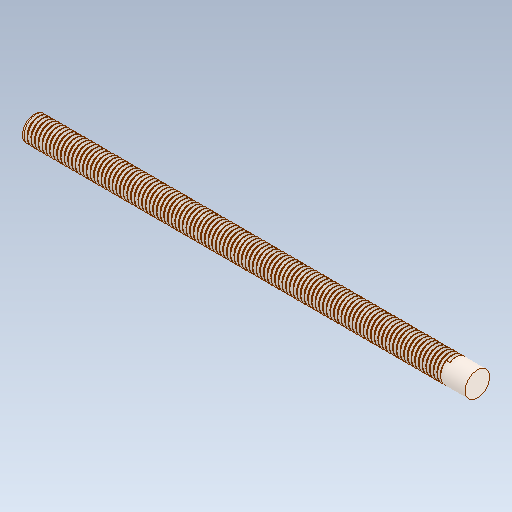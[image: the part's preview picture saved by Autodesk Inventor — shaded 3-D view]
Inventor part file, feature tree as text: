
AUTODESK INVENTOR PART (.ipt)
format: ipt  version: 2021 (Build 250183000, 183)  size: 810,496 bytes
history: mixed  units: mm
features: other x1, thread x1, imported_body x1
ambient origin geometry x8: Origin, YZ Plane, XZ Plane, XY Plane, X Axis, Y Axis, Z Axis, Center Point
bodies: Body1 (imported_parasolid)
feature tree (3):
  other  "Sólido1"
  thread  "Rosca1"  [1 undecoded]
  imported_body  NMx_Import_Brep_tag  [imported B-rep: ~7 faces, bbox_mm=[0.0, 0.0, 0.0]]
note: 1 required parameter value undecoded (feature->parameter linkage not recoverable at this tier; creation-order binding heuristic only, values carry confidence <= 0.55)
